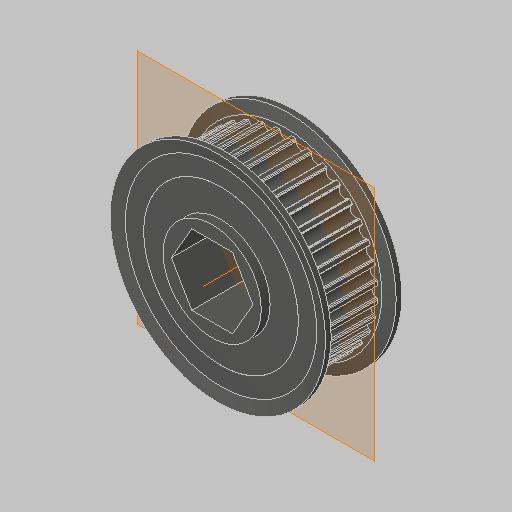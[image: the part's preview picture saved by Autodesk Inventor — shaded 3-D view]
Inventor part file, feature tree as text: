
AUTODESK INVENTOR PART (.ipt)
format: ipt  version: 2023.5 (Build 275446000, 446)  size: 404,480 bytes
history: native  units: in
note: dims shown in document units (in); Inventor stores cm internally (conversion verified against a paired STEP export)
features: revolve x2, other x1
ambient origin geometry x8: Origin, YZ Plane, XZ Plane, XY Plane, X Axis, Y Axis, Z Axis, Center Point
bodies: Solid1 (feature_tree), Solid2 (feature_tree), Solid3 (feature_tree)
feature tree (3):
  revolve  "Revolve1[1]"  [1 undecoded]
  revolve  "Revolve1[2]"  [1 undecoded]
  other  "Cut-Extrude4"
note: 2 required parameter values undecoded (feature->parameter linkage not recoverable at this tier; creation-order binding heuristic only, values carry confidence <= 0.55)
